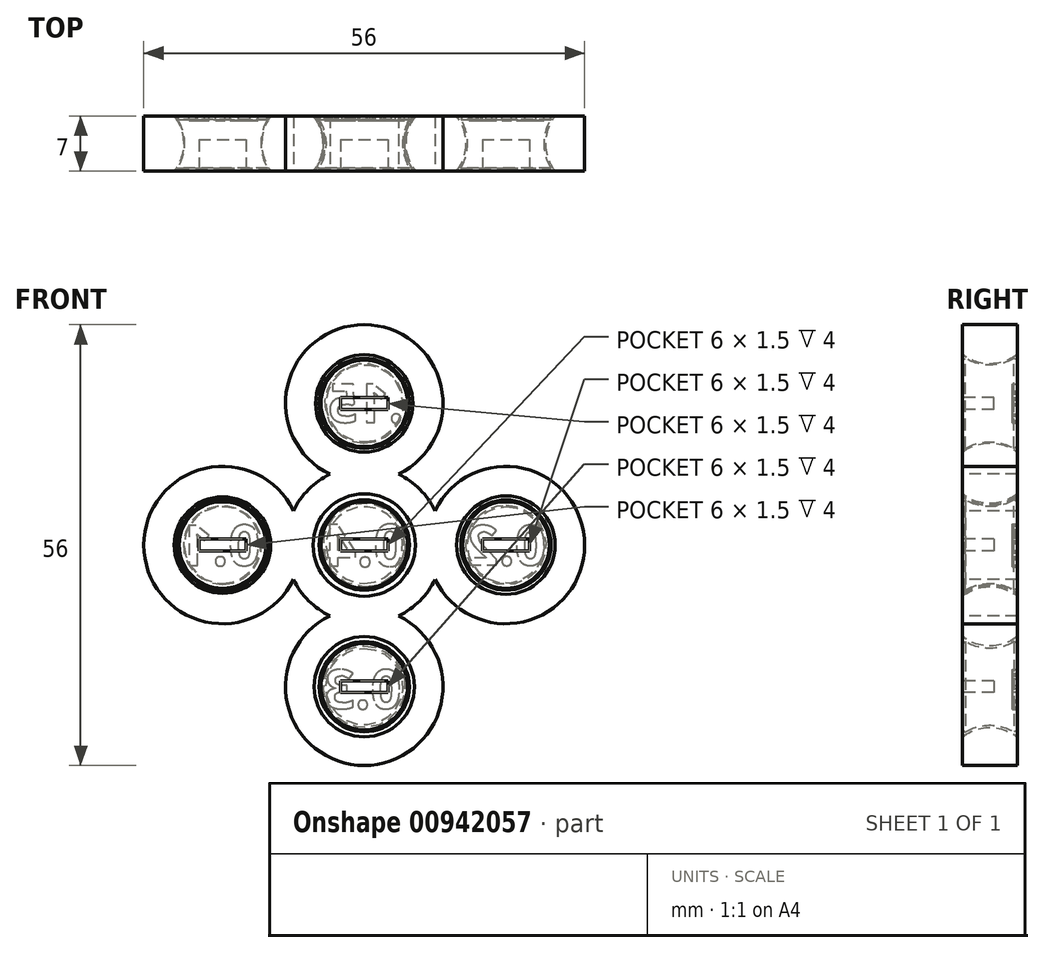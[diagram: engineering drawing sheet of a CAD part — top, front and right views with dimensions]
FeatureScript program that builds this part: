
annotation { "Feature Type Name" : "Feature", "Feature Type Description" : "" }
export const myFeature = defineFeature(function(context is Context, id is Id, definition is map)
    precondition{}
    {
        {
            var Q0;
            Q0=qCreatedBy(makeId("Top.planeOp"),FACE);
            var sketch = newSketch(context, id + "F0", { "sketchPlane" : qUnion([Q0])});
            skLineSegment(sketch, "E0.bottom", {"start": v(-24, 0) * mm, "end": v(-18, 0) * mm});
            skLineSegment(sketch, "E0.top", {"start": v(-24, 7) * mm, "end": v(-18, 7) * mm});
            skLineSegment(sketch, "E0.right", {"start": v(-18, 0) * mm, "end": v(-18, 7) * mm});
            skArc(sketch, "E1", {"start": v(-24, 0) * mm, "mid": v(-22.87, 3.5) * mm, "end": v(-24, 7) * mm});
            skArc(sketch, "E2.0", {"start": v(-24.12, 0) * mm, "mid": v(-22.97, 3.5) * mm, "end": v(-24.12, 7) * mm});
            skLineSegment(sketch, "E3", {"start": v(-24.12, 0) * mm, "end": v(-24, 0) * mm, "construction": true});
            skLineSegment(sketch, "E4", {"start": v(-24.12, 0) * mm, "end": v(-28, 0) * mm});
            skLineSegment(sketch, "E5", {"start": v(-28, 0) * mm, "end": v(-28, 7) * mm});
            skLineSegment(sketch, "E6", {"start": v(-28, 7) * mm, "end": v(-24.12, 7) * mm});
            skPoint(sketch, "E7", {"position": v(0, 0) * mm});
            skLineSegment(sketch, "E8", {"start": v(-28.87, 3.5) * mm, "end": v(-28, 3.5) * mm, "construction": true});
            skLineSegment(sketch, "E9.trimOffspring", {"start": v(-24, 7) * mm, "end": v(-24.12, 7) * mm, "construction": true});
            skLineSegment(sketch, "E10", {"start": v(0, 0) * mm, "end": v(-18, 0) * mm, "construction": true});
            skPoint(sketch, "E11", {"position": v(-23.5, 0) * mm});
            skPoint(sketch, "E12", {"position": v(-23.73, 0.42) * mm});
            skLineSegment(sketch, "E13", {"start": v(-23.73, 0.42) * mm, "end": v(-23.5, 0) * mm});
            skPoint(sketch, "E14", {"position": v(-23.5, 7) * mm});
            skPoint(sketch, "E15", {"position": v(-23.73, 6.58) * mm});
            skLineSegment(sketch, "E16", {"start": v(-23.5, 7) * mm, "end": v(-23.73, 6.58) * mm});
            skSolve(sketch);
        }
        {
            var Q0;
            {var subQ0=sQuery(id+"F0.wireOp",EDGE,"E0.right");Q0=makeQuery(id+"F0.imprint","IMPRINT",FACE,{"disambiguationData":[TD([[makeQuery(id+"F0.imprint","IMPRINT",EDGE,{"derivedFrom":subQ0}),1.0]])]});}
            var Q1;
            Q1=makeQuery(id+"F0.imprint","IMPRINT",FACE,{"disambiguationData":[TD([[makeQuery(id+"F0.imprint","IMPRINT",EDGE,{"derivedFrom":sQuery(id+"F0.wireOp",EDGE,"E2.0")}),1.0]])]});
            var Q2;
            Q2=sQuery(id+"F0.wireOp",EDGE,"E0.right");
            revolve(context, id + "F1", {"surfaceOperationType" : NewSurfaceOperationType.NEW, "entities" : qUnion([Q0, Q1]), "axis" : qUnion([Q2]), "revolveType" : RevolveType.FULL});
        }
        {
            var Q0;
            Q0=qCreatedBy(makeId("Right.planeOp"),FACE);
            var sketch = newSketch(context, id + "F2", { "sketchPlane" : qUnion([Q0])});
            skLineSegment(sketch, "E17.bottom", {"start": v(0, 24) * mm, "end": v(0, 18) * mm});
            skLineSegment(sketch, "E17.top", {"start": v(7, 24) * mm, "end": v(7, 18) * mm});
            skLineSegment(sketch, "E17.right", {"start": v(0, 18) * mm, "end": v(7, 18) * mm});
            skArc(sketch, "E18", {"start": v(0, 24) * mm, "mid": v(3.5, 22.87) * mm, "end": v(7, 24) * mm});
            skArc(sketch, "E19.0", {"start": v(0, 24.19) * mm, "mid": v(3.5, 23.02) * mm, "end": v(7, 24.19) * mm});
            skLineSegment(sketch, "E20", {"start": v(0, 24.19) * mm, "end": v(0, 24) * mm, "construction": true});
            skLineSegment(sketch, "E21", {"start": v(0, 24.19) * mm, "end": v(0, 28) * mm});
            skLineSegment(sketch, "E22", {"start": v(0, 28) * mm, "end": v(7, 28) * mm});
            skLineSegment(sketch, "E23", {"start": v(7, 28) * mm, "end": v(7, 24.19) * mm});
            skPoint(sketch, "E24", {"position": v(0, 0) * mm});
            skLineSegment(sketch, "E25", {"start": v(3.5, 28.87) * mm, "end": v(3.5, 28) * mm, "construction": true});
            skLineSegment(sketch, "E26.trimOffspring", {"start": v(7, 24) * mm, "end": v(7, 24.19) * mm, "construction": true});
            skLineSegment(sketch, "E27", {"start": v(0, 0) * mm, "end": v(0, 18) * mm, "construction": true});
            skPoint(sketch, "E28", {"position": v(7, 23.5) * mm});
            skPoint(sketch, "E29", {"position": v(6.58, 23.73) * mm});
            skPoint(sketch, "E30", {"position": v(0.42, 23.73) * mm});
            skPoint(sketch, "E31", {"position": v(0, 23.5) * mm});
            skLineSegment(sketch, "E32", {"start": v(7, 23.5) * mm, "end": v(6.58, 23.73) * mm});
            skLineSegment(sketch, "E33", {"start": v(0.42, 23.73) * mm, "end": v(0, 23.5) * mm});
            skSolve(sketch);
        }
        {
            var Q0;
            {var subQ0=sQuery(id+"F2.wireOp",EDGE,"E17.right");Q0=makeQuery(id+"F2.imprint","IMPRINT",FACE,{"disambiguationData":[TD([[makeQuery(id+"F2.imprint","IMPRINT",EDGE,{"derivedFrom":subQ0}),1.0]])]});}
            var Q1;
            Q1=makeQuery(id+"F2.imprint","IMPRINT",FACE,{"disambiguationData":[TD([[makeQuery(id+"F2.imprint","IMPRINT",EDGE,{"derivedFrom":sQuery(id+"F2.wireOp",EDGE,"E19.0")}),1.0]])]});
            var Q2;
            Q2=sQuery(id+"F2.wireOp",EDGE,"E17.right");
            revolve(context, id + "F3", {"surfaceOperationType" : NewSurfaceOperationType.NEW, "entities" : qUnion([Q0, Q1]), "axis" : qUnion([Q2]), "revolveType" : RevolveType.FULL});
        }
        {
            var Q0;
            Q0=qCreatedBy(makeId("Top.planeOp"),FACE);
            var sketch = newSketch(context, id + "F4", { "sketchPlane" : qUnion([Q0])});
            skLineSegment(sketch, "E34.bottom", {"start": v(24, 7) * mm, "end": v(18, 7) * mm});
            skLineSegment(sketch, "E34.top", {"start": v(24, 0) * mm, "end": v(18, 0) * mm});
            skLineSegment(sketch, "E34.right", {"start": v(18, 7) * mm, "end": v(18, 0) * mm});
            skArc(sketch, "E35", {"start": v(24, 7) * mm, "mid": v(22.87, 3.5) * mm, "end": v(24, 0) * mm});
            skArc(sketch, "E36.0", {"start": v(24.25, 7) * mm, "mid": v(23.07, 3.5) * mm, "end": v(24.25, 0) * mm});
            skLineSegment(sketch, "E37", {"start": v(24.25, 7) * mm, "end": v(24, 7) * mm, "construction": true});
            skLineSegment(sketch, "E38", {"start": v(24.25, 7) * mm, "end": v(28, 7) * mm});
            skLineSegment(sketch, "E39", {"start": v(28, 7) * mm, "end": v(28, 0) * mm});
            skLineSegment(sketch, "E40", {"start": v(28, 0) * mm, "end": v(24.25, 0) * mm});
            skPoint(sketch, "E41", {"position": v(0, 7) * mm});
            skLineSegment(sketch, "E42", {"start": v(28.87, 3.5) * mm, "end": v(28, 3.5) * mm, "construction": true});
            skLineSegment(sketch, "E43.trimOffspring", {"start": v(24, 0) * mm, "end": v(24.25, 0) * mm, "construction": true});
            skLineSegment(sketch, "E44", {"start": v(0, 7) * mm, "end": v(18, 7) * mm, "construction": true});
            skPoint(sketch, "E45", {"position": v(23.5, 7) * mm});
            skPoint(sketch, "E46", {"position": v(23.73, 6.58) * mm});
            skPoint(sketch, "E47", {"position": v(23.73, 0.42) * mm});
            skPoint(sketch, "E48", {"position": v(23.5, 0) * mm});
            skLineSegment(sketch, "E49", {"start": v(23.5, 7) * mm, "end": v(23.73, 6.58) * mm});
            skLineSegment(sketch, "E50", {"start": v(23.73, 0.42) * mm, "end": v(23.5, 0) * mm});
            skSolve(sketch);
        }
        {
            var Q0;
            {var subQ3=sQuery(id+"F4.wireOp",EDGE,"E34.right");Q0=makeQuery(id+"F4.imprint","IMPRINT",FACE,{"disambiguationData":[TD([[makeQuery(id+"F4.imprint","IMPRINT",EDGE,{"derivedFrom":subQ3}),1.0]])]});}
            var Q1;
            Q1=makeQuery(id+"F4.imprint","IMPRINT",FACE,{"disambiguationData":[TD([[makeQuery(id+"F4.imprint","IMPRINT",EDGE,{"derivedFrom":sQuery(id+"F4.wireOp",EDGE,"E36.0")}),1.0]])]});
            var Q2;
            Q2=sQuery(id+"F4.wireOp",EDGE,"E34.right");
            revolve(context, id + "F5", {"surfaceOperationType" : NewSurfaceOperationType.NEW, "entities" : qUnion([Q0, Q1]), "axis" : qUnion([Q2]), "revolveType" : RevolveType.FULL});
        }
        {
            var Q0;
            Q0=qCreatedBy(makeId("Right.planeOp"),FACE);
            var sketch = newSketch(context, id + "F6", { "sketchPlane" : qUnion([Q0])});
            skLineSegment(sketch, "E51.bottom", {"start": v(7, -24) * mm, "end": v(7, -18) * mm});
            skLineSegment(sketch, "E51.top", {"start": v(0, -24) * mm, "end": v(0, -18) * mm});
            skLineSegment(sketch, "E51.right", {"start": v(7, -18) * mm, "end": v(0, -18) * mm});
            skArc(sketch, "E52", {"start": v(7, -24) * mm, "mid": v(3.5, -22.87) * mm, "end": v(0, -24) * mm});
            skArc(sketch, "E53.0", {"start": v(7, -24.37) * mm, "mid": v(3.5, -23.17) * mm, "end": v(0, -24.37) * mm});
            skLineSegment(sketch, "E54", {"start": v(7, -24.37) * mm, "end": v(7, -24) * mm, "construction": true});
            skLineSegment(sketch, "E55", {"start": v(7, -24.37) * mm, "end": v(7, -28) * mm});
            skLineSegment(sketch, "E56", {"start": v(7, -28) * mm, "end": v(0, -28) * mm});
            skLineSegment(sketch, "E57", {"start": v(0, -28) * mm, "end": v(0, -24.37) * mm});
            skLineSegment(sketch, "E58", {"start": v(3.5, -28.87) * mm, "end": v(3.5, -28) * mm, "construction": true});
            skLineSegment(sketch, "E59.trimOffspring", {"start": v(0, -24) * mm, "end": v(0, -24.37) * mm, "construction": true});
            skLineSegment(sketch, "E60", {"start": v(6.58, -23.73) * mm, "end": v(7, -23.5) * mm});
            skLineSegment(sketch, "E61", {"start": v(0.42, -23.73) * mm, "end": v(0, -23.5) * mm});
            skSolve(sketch);
        }
        {
            var Q0;
            {var subQ3=sQuery(id+"F6.wireOp",EDGE,"E51.right");Q0=makeQuery(id+"F6.imprint","IMPRINT",FACE,{"disambiguationData":[TD([[makeQuery(id+"F6.imprint","IMPRINT",EDGE,{"derivedFrom":subQ3}),1.0]])]});}
            var Q1;
            Q1=makeQuery(id+"F6.imprint","IMPRINT",FACE,{"disambiguationData":[TD([[makeQuery(id+"F6.imprint","IMPRINT",EDGE,{"derivedFrom":sQuery(id+"F6.wireOp",EDGE,"E53.0")}),1.0]])]});
            var Q2;
            Q2=sQuery(id+"F6.wireOp",EDGE,"E51.right");
            revolve(context, id + "F7", {"surfaceOperationType" : NewSurfaceOperationType.NEW, "entities" : qUnion([Q0, Q1]), "axis" : qUnion([Q2]), "revolveType" : RevolveType.FULL});
        }
        {
            var Q0;
            Q0=qCreatedBy(makeId("Right.planeOp"),FACE);
            cPlane(context, id + "F8", {"entities" : qUnion([Q0]), "cplaneType" : CPlaneType.OFFSET, "offset" : 0 * mm, "width" : 150 * mm, "height" : 150 * mm});
        }
        {
            var Q0;
            Q0=qCreatedBy(id+"F8.planeOp",FACE);
            var sketch = newSketch(context, id + "F9", { "sketchPlane" : qUnion([Q0])});
            skLineSegment(sketch, "E62.bottom", {"start": v(0, 6) * mm, "end": v(0, 0) * mm});
            skLineSegment(sketch, "E62.top", {"start": v(7, 6) * mm, "end": v(7, 0) * mm});
            skLineSegment(sketch, "E62.right", {"start": v(0, 0) * mm, "end": v(7, 0) * mm});
            skArc(sketch, "E63", {"start": v(0, 6) * mm, "mid": v(3.5, 4.87) * mm, "end": v(7, 6) * mm});
            skArc(sketch, "E64.0", {"start": v(0, 6.5) * mm, "mid": v(3.5, 5.27) * mm, "end": v(7, 6.5) * mm});
            skLineSegment(sketch, "E65", {"start": v(0, 6.5) * mm, "end": v(0, 6) * mm, "construction": true});
            skLineSegment(sketch, "E66", {"start": v(0, 6.5) * mm, "end": v(0, 10) * mm});
            skLineSegment(sketch, "E67", {"start": v(0, 10) * mm, "end": v(7, 10) * mm});
            skLineSegment(sketch, "E68", {"start": v(7, 10) * mm, "end": v(7, 6.5) * mm});
            skLineSegment(sketch, "E69", {"start": v(3.5, 10.87) * mm, "end": v(3.5, 10) * mm, "construction": true});
            skLineSegment(sketch, "E70.trimOffspring", {"start": v(7, 6) * mm, "end": v(7, 6.5) * mm, "construction": true});
            skLineSegment(sketch, "E71", {"start": v(7, 5.5) * mm, "end": v(6.58, 5.73) * mm});
            skLineSegment(sketch, "E72", {"start": v(0.42, 5.73) * mm, "end": v(0, 5.5) * mm});
            skSolve(sketch);
        }
        {
            var Q0;
            {var subQ0=sQuery(id+"F9.wireOp",EDGE,"E62.right");Q0=makeQuery(id+"F9.imprint","IMPRINT",FACE,{"disambiguationData":[TD([[makeQuery(id+"F9.imprint","IMPRINT",EDGE,{"derivedFrom":subQ0}),1.0]])]});}
            var Q1;
            Q1=makeQuery(id+"F9.imprint","IMPRINT",FACE,{"disambiguationData":[TD([[makeQuery(id+"F9.imprint","IMPRINT",EDGE,{"derivedFrom":sQuery(id+"F9.wireOp",EDGE,"E64.0")}),1.0]])]});
            var Q2;
            Q2=sQuery(id+"F9.wireOp",EDGE,"E62.right");
            revolve(context, id + "F10", {"operationType" : NewBodyOperationType.ADD, "surfaceOperationType" : NewSurfaceOperationType.NEW, "entities" : qUnion([Q0, Q1]), "axis" : qUnion([Q2]), "revolveType" : RevolveType.FULL});
        }
        {
            var Q0;
            Q0=makeQuery(id+"F1.opRevolve","SWEPT_FACE",FACE,{"disambiguationData":[OSD([sQuery(id+"F0.wireOp",EDGE,"E0.top")])]});
            var sketch = newSketch(context, id + "F11", { "sketchPlane" : qUnion([Q0])});
            skText(sketch, "E73", { "text": "0.1", "fontName": "OpenSans-Bold.ttf"});
            skText(sketch, "E74", { "text": ".15", "fontName": "OpenSans-Bold.ttf"});
            skText(sketch, "E75", { "text": "0.2", "fontName": "OpenSans-Bold.ttf"});
            skText(sketch, "E76", { "text": "0.3", "fontName": "OpenSans-Bold.ttf"});
            skText(sketch, "E77", { "text": "0.4", "fontName": "OpenSans-Bold.ttf"});
            const initialGuessF11  = {"E73": [0.0132, -0.00258, 1, 0, 0.00514], "E74": [-0.00501, 0.0156, 1, 0, 0.00488], "E75": [-0.0231, -0.00254, 1, 0, 0.00505], "E76": [-0.00472, -0.02077, 1, 0, 0.00495], "E77": [-0.00537, -0.00267, 1, 0, 0.00532]};
            skSetInitialGuess(sketch, initialGuessF11);
            skSolve(sketch);
        }
        {
            var Q0;
            Q0 = qSketchRegion(id + "F11", true);
            extrude(context, id + "F12", {"entities" : qUnion([Q0]), "operationType" : NewBodyOperationType.REMOVE, "oppositeDirection" : true, "depth" : 0.6 * mm, "offsetDistance" : 25 * mm});
        }
        {
            var Q0;
            Q0=makeQuery(id+"F10.boolean.opBoolean","MERGE",FACE,{"derivedFrom":[makeQuery(id+"F1.opRevolve","SWEPT_FACE",FACE,{"disambiguationData":[OSD([sQuery(id+"F0.wireOp",EDGE,"E4")])]}),makeQuery(id+"F3.opRevolve","SWEPT_FACE",FACE,{"disambiguationData":[OSD([sQuery(id+"F2.wireOp",EDGE,"E21")])]}),makeQuery(id+"F5.opRevolve","SWEPT_FACE",FACE,{"disambiguationData":[OSD([sQuery(id+"F4.wireOp",EDGE,"E40")])]}),makeQuery(id+"F7.opRevolve","SWEPT_FACE",FACE,{"disambiguationData":[OSD([sQuery(id+"F6.wireOp",EDGE,"E57")])]}),makeQuery(id+"F10.opRevolve","SWEPT_FACE",FACE,{"disambiguationData":[OSD([sQuery(id+"F9.wireOp",EDGE,"E66")])]})]});
            var sketch = newSketch(context, id + "F13", { "sketchPlane" : qUnion([Q0])});
            skLineSegment(sketch, "E78.bottom", {"start": v(-21, 0.75) * mm, "end": v(-15, 0.75) * mm});
            skLineSegment(sketch, "E78.top", {"start": v(-21, -0.75) * mm, "end": v(-15, -0.75) * mm});
            skLineSegment(sketch, "E78.left", {"start": v(-21, 0.75) * mm, "end": v(-21, -0.75) * mm});
            skLineSegment(sketch, "E78.right", {"start": v(-15, 0.75) * mm, "end": v(-15, -0.75) * mm});
            skPoint(sketch, "E78.middle", {"position": v(-18, 0) * mm});
            skLineSegment(sketch, "E79.bottom", {"start": v(-3, 0.75) * mm, "end": v(3, 0.75) * mm});
            skLineSegment(sketch, "E79.top", {"start": v(-3, -0.75) * mm, "end": v(3, -0.75) * mm});
            skLineSegment(sketch, "E79.left", {"start": v(-3, 0.75) * mm, "end": v(-3, -0.75) * mm});
            skLineSegment(sketch, "E79.right", {"start": v(3, 0.75) * mm, "end": v(3, -0.75) * mm});
            skPoint(sketch, "E79.middle", {"position": v(0, 0) * mm});
            skLineSegment(sketch, "E80.bottom", {"start": v(-3, 17.25) * mm, "end": v(3, 17.25) * mm});
            skLineSegment(sketch, "E80.top", {"start": v(-3, 18.75) * mm, "end": v(3, 18.75) * mm});
            skLineSegment(sketch, "E80.left", {"start": v(-3, 17.25) * mm, "end": v(-3, 18.75) * mm});
            skLineSegment(sketch, "E80.right", {"start": v(3, 17.25) * mm, "end": v(3, 18.75) * mm});
            skPoint(sketch, "E80.middle", {"position": v(0, 18) * mm});
            skLineSegment(sketch, "E81.bottom", {"start": v(15, 0.75) * mm, "end": v(21, 0.75) * mm});
            skLineSegment(sketch, "E81.top", {"start": v(15, -0.75) * mm, "end": v(21, -0.75) * mm});
            skLineSegment(sketch, "E81.left", {"start": v(15, 0.75) * mm, "end": v(15, -0.75) * mm});
            skLineSegment(sketch, "E81.right", {"start": v(21, 0.75) * mm, "end": v(21, -0.75) * mm});
            skPoint(sketch, "E81.middle", {"position": v(18, 0) * mm});
            skLineSegment(sketch, "E82.bottom", {"start": v(-3, -17.25) * mm, "end": v(3, -17.25) * mm});
            skLineSegment(sketch, "E82.top", {"start": v(-3, -18.75) * mm, "end": v(3, -18.75) * mm});
            skLineSegment(sketch, "E82.left", {"start": v(-3, -17.25) * mm, "end": v(-3, -18.75) * mm});
            skLineSegment(sketch, "E82.right", {"start": v(3, -17.25) * mm, "end": v(3, -18.75) * mm});
            skPoint(sketch, "E82.middle", {"position": v(0, -18) * mm});
            skSolve(sketch);
        }
        {
            var Q0;
            Q0 = qSketchRegion(id + "F13", true);
            extrude(context, id + "F14", {"entities" : qUnion([Q0]), "operationType" : NewBodyOperationType.REMOVE, "oppositeDirection" : true, "depth" : 4 * mm, "offsetDistance" : 25 * mm});
        }
    });
